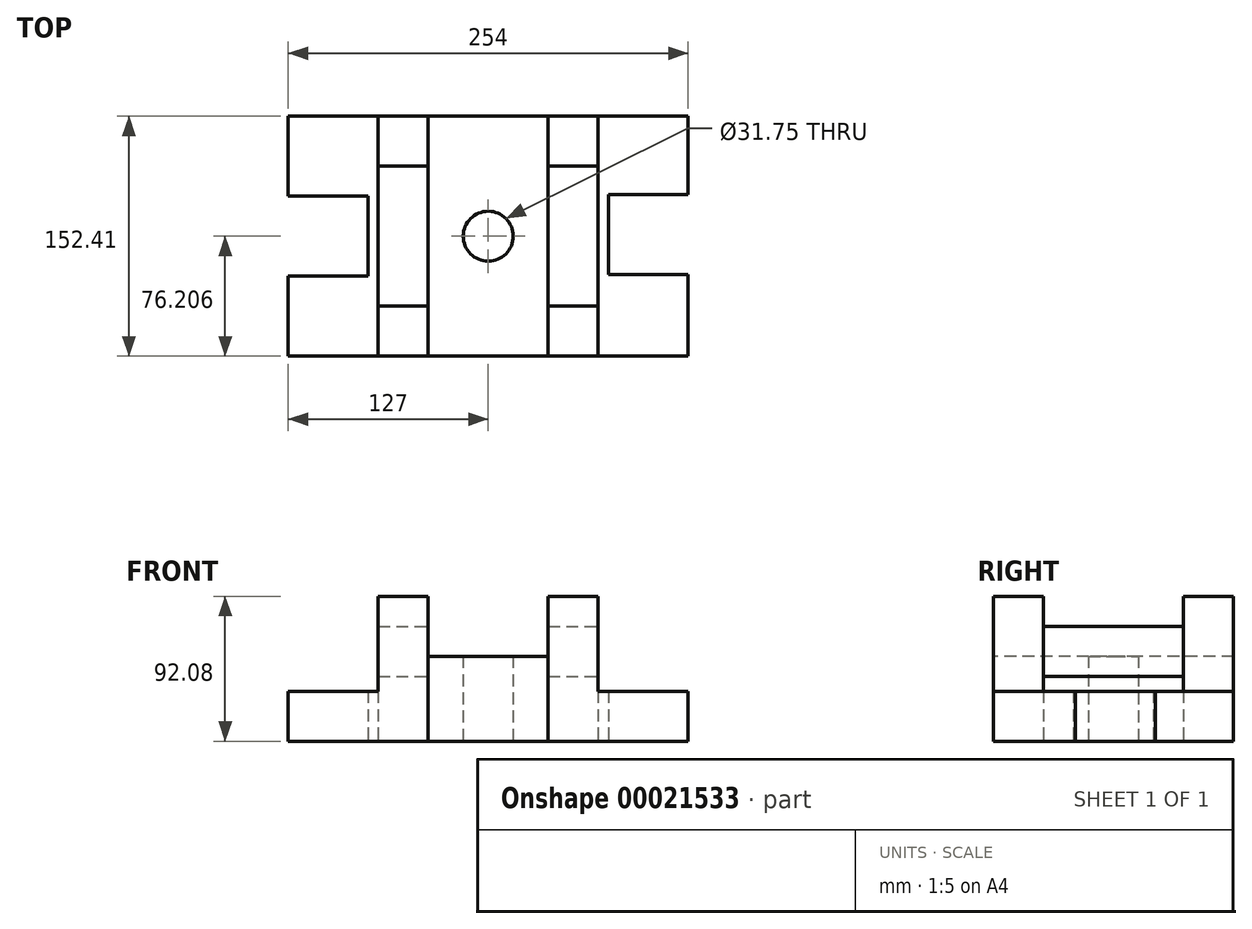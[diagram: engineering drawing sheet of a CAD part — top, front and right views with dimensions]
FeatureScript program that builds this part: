
annotation { "Feature Type Name" : "Feature", "Feature Type Description" : "" }
export const myFeature = defineFeature(function(context is Context, id is Id, definition is map)
    precondition{}
    {
        {
            var Q0;
            Q0=qCreatedBy(makeId("Top.planeOp"),FACE);
            var sketch = newSketch(context, id + "F0", { "sketchPlane" : qUnion([Q0])});
            skLineSegment(sketch, "E0.bottom", {"start": v(69.85, 100.56) * mm, "end": v(127, 100.56) * mm});
            skLineSegment(sketch, "E0.top", {"start": v(0, -51.84) * mm, "end": v(127, -51.84) * mm});
            skLineSegment(sketch, "E0.right", {"start": v(127, 100.56) * mm, "end": v(127, -51.84) * mm});
            skLineSegment(sketch, "E1", {"start": v(127, 50.8) * mm, "end": v(76.38, 50.8) * mm});
            skLineSegment(sketch, "E2", {"start": v(76.38, 50.8) * mm, "end": v(76.38, 0) * mm});
            skLineSegment(sketch, "E3", {"start": v(76.38, 0) * mm, "end": v(127, 0) * mm});
            skLineSegment(sketch, "E4", {"start": v(38.1, 68.8) * mm, "end": v(38.1, -20.1) * mm});
            skLineSegment(sketch, "E5", {"start": v(69.85, 68.8) * mm, "end": v(69.85, -20.1) * mm});
            skLineSegment(sketch, "E6", {"start": v(0, 100.56) * mm, "end": v(38.1, 100.56) * mm});
            skLineSegment(sketch, "E7", {"start": v(38.1, 100.56) * mm, "end": v(69.85, 100.56) * mm});
            skLineSegment(sketch, "E8.MirrorCS", {"start": v(0, 100.55) * mm, "end": v(-38.1, 100.55) * mm});
            skLineSegment(sketch, "E9.MirrorCS", {"start": v(-38.1, 68.8) * mm, "end": v(-38.1, -20.1) * mm});
            skLineSegment(sketch, "E10.MirrorCS", {"start": v(-69.85, 68.8) * mm, "end": v(-69.85, -20.1) * mm});
            skLineSegment(sketch, "E11.MirrorCS", {"start": v(0, -51.85) * mm, "end": v(-127, -51.85) * mm});
            skLineSegment(sketch, "E12.MirrorCS", {"start": v(-127, 100.55) * mm, "end": v(-127, 100.55) * mm});
            skLineSegment(sketch, "E13.MirrorCS", {"start": v(-76.38, 50.8) * mm, "end": v(-76.38, -0.9) * mm});
            skLineSegment(sketch, "E14.MirrorCS", {"start": v(-127, 49.75) * mm, "end": v(-76.38, 49.75) * mm});
            skLineSegment(sketch, "E15.MirrorCS", {"start": v(-69.85, 100.55) * mm, "end": v(-127, 100.55) * mm});
            skLineSegment(sketch, "E16", {"start": v(0, -51.84) * mm, "end": v(0, 24.36) * mm});
            skLineSegment(sketch, "E17", {"start": v(-69.85, 68.8) * mm, "end": v(-38.1, 68.8) * mm});
            skLineSegment(sketch, "E18", {"start": v(38.1, 68.8) * mm, "end": v(69.85, 68.8) * mm});
            skLineSegment(sketch, "E19", {"start": v(-69.85, -20.1) * mm, "end": v(-38.1, -20.1) * mm});
            skLineSegment(sketch, "E20", {"start": v(38.1, -20.1) * mm, "end": v(69.85, -20.1) * mm});
            skLineSegment(sketch, "E21", {"start": v(38.1, 100.56) * mm, "end": v(38.1, 68.8) * mm});
            skLineSegment(sketch, "E22", {"start": v(69.85, 100.56) * mm, "end": v(69.85, 68.8) * mm});
            skLineSegment(sketch, "E23", {"start": v(38.1, -20.1) * mm, "end": v(38.1, -51.84) * mm});
            skLineSegment(sketch, "E24", {"start": v(69.85, -20.1) * mm, "end": v(69.85, -51.84) * mm});
            skLineSegment(sketch, "E25", {"start": v(-69.85, 100.55) * mm, "end": v(-69.85, 68.8) * mm});
            skLineSegment(sketch, "E26", {"start": v(-38.1, 100.55) * mm, "end": v(-38.1, 68.8) * mm});
            skLineSegment(sketch, "E27", {"start": v(-38.1, -20.1) * mm, "end": v(-38.1, -51.85) * mm});
            skLineSegment(sketch, "E28", {"start": v(-69.85, -20.1) * mm, "end": v(-69.85, -51.85) * mm});
            skLineSegment(sketch, "E29.trimOffspring", {"start": v(-127, 49.75) * mm, "end": v(-127, -1.05) * mm});
            skLineSegment(sketch, "E30", {"start": v(-127, 100.55) * mm, "end": v(-127, 49.75) * mm});
            skLineSegment(sketch, "E31", {"start": v(-127, -1.05) * mm, "end": v(-127, -51.85) * mm});
            skLineSegment(sketch, "E32", {"start": v(-69.85, 100.55) * mm, "end": v(-38.1, 100.55) * mm});
            skLineSegment(sketch, "E33", {"start": v(-76.38, 49.75) * mm, "end": v(-69.85, 49.75) * mm});
            skLineSegment(sketch, "E34", {"start": v(-76.38, -0.9) * mm, "end": v(-69.85, -0.9) * mm});
            skLineSegment(sketch, "E35", {"start": v(-145.92, 92.06) * mm, "end": v(-145.92, 94.46) * mm});
            skLineSegment(sketch, "E36", {"start": v(-76.38, -0.9) * mm, "end": v(-127, -1.05) * mm});
            skLineSegment(sketch, "E37.bottom", {"start": v(-38.1, 100.55) * mm, "end": v(38.1, 100.55) * mm});
            skLineSegment(sketch, "E37.top", {"start": v(-38.1, -51.84) * mm, "end": v(38.1, -51.84) * mm});
            skLineSegment(sketch, "E37.left", {"start": v(-38.1, 100.55) * mm, "end": v(-38.1, -51.84) * mm});
            skLineSegment(sketch, "E37.right", {"start": v(38.1, 100.55) * mm, "end": v(38.1, -51.84) * mm});
            skCircle(sketch, "E38", {"center": v(0, 24.36) * mm, "radius": 15.88 * mm});
            skSolve(sketch);
        }
        {
            var Q0;
            {var subQ6=sQuery(id+"F0.wireOp",EDGE,"E0.bottom");Q0=makeQuery(id+"F0.imprint","IMPRINT",FACE,{"disambiguationData":[TD([[makeQuery(id+"F0.imprint","IMPRINT",EDGE,{"derivedFrom":subQ6}),-1.0]])]});}
            extrude(context, id + "F1", {"entities" : qUnion([Q0]), "depth" : 31.75 * mm});
        }
        {
            var Q0;
            Q0=makeQuery(id+"F0.imprint","IMPRINT",FACE,{"disambiguationData":[TD([[makeQuery(id+"F0.imprint","IMPRINT",EDGE,{"derivedFrom":sQuery(id+"F0.wireOp",EDGE,"E20")}),-1.0]])]});
            var Q1;
            Q1=makeQuery(id+"F0.imprint","IMPRINT",FACE,{"disambiguationData":[TD([[makeQuery(id+"F0.imprint","IMPRINT",EDGE,{"derivedFrom":sQuery(id+"F0.wireOp",EDGE,"E7")}),-1.0]])]});
            extrude(context, id + "F2", {"entities" : qUnion([Q0, Q1]), "operationType" : NewBodyOperationType.ADD, "depth" : 92.07 * mm});
        }
        {
            var Q0;
            Q0=makeQuery(id+"F0.imprint","IMPRINT",FACE,{"disambiguationData":[TD([[makeQuery(id+"F0.imprint","IMPRINT",EDGE,{"derivedFrom":sQuery(id+"F0.wireOp",EDGE,"E4")}),1.0]])]});
            extrude(context, id + "F3", {"entities" : qUnion([Q0]), "operationType" : NewBodyOperationType.ADD, "depth" : 41.27 * mm});
        }
        {
            var Q0;
            Q0=makeQuery(id+"F0.imprint","IMPRINT",FACE,{"disambiguationData":[TD([[makeQuery(id+"F0.imprint","IMPRINT",EDGE,{"derivedFrom":sQuery(id+"F0.wireOp",EDGE,"E15.MirrorCS")}),1.0]])]});
            var Q1;
            {var subQ1=sQuery(id+"F0.wireOp",EDGE,"E33");Q1=makeQuery(id+"F0.imprint","IMPRINT",FACE,{"disambiguationData":[TD([[makeQuery(id+"F0.imprint","IMPRINT",EDGE,{"derivedFrom":subQ1}),-1.0]])]});}
            var Q2;
            {var subQ2=sQuery(id+"F0.wireOp",EDGE,"E28");Q2=makeQuery(id+"F0.imprint","IMPRINT",FACE,{"disambiguationData":[TD([[makeQuery(id+"F0.imprint","IMPRINT",EDGE,{"derivedFrom":subQ2}),-1.0]])]});}
            extrude(context, id + "F4", {"entities" : qUnion([Q0, Q1, Q2]), "depth" : 31.75 * mm});
        }
        {
            var Q0;
            Q0=makeQuery(id+"F0.imprint","IMPRINT",FACE,{"disambiguationData":[TD([[makeQuery(id+"F0.imprint","IMPRINT",EDGE,{"derivedFrom":sQuery(id+"F0.wireOp",EDGE,"E17")}),1.0]])]});
            var Q1;
            Q1=makeQuery(id+"F0.imprint","IMPRINT",FACE,{"disambiguationData":[TD([[makeQuery(id+"F0.imprint","IMPRINT",EDGE,{"derivedFrom":sQuery(id+"F0.wireOp",EDGE,"E19")}),-1.0]])]});
            extrude(context, id + "F5", {"entities" : qUnion([Q0, Q1]), "operationType" : NewBodyOperationType.ADD, "depth" : 92.07 * mm});
        }
        {
            var Q0;
            Q0=makeQuery(id+"F0.imprint","IMPRINT",FACE,{"disambiguationData":[TD([[makeQuery(id+"F0.imprint","IMPRINT",EDGE,{"derivedFrom":sQuery(id+"F0.wireOp",EDGE,"E9.MirrorCS")}),-1.0]])]});
            extrude(context, id + "F6", {"entities" : qUnion([Q0]), "operationType" : NewBodyOperationType.ADD, "depth" : 41.27 * mm});
        }
        {
            var Q0;
            {var subQ2=sQuery(id+"F0.wireOp",EDGE,"E37.top");var subQ11=makeQuery(id+"F0.imprint","IMPRINT",VERTEX,{"derivedFrom":subQ2});Q0=makeQuery(id+"F0.imprint","IMPRINT",FACE,{"disambiguationData":[TD([[makeQuery(id+"F0.imprint","IMPRINT",EDGE,{"disambiguationData":[TD([[subQ11,1.0]])],"derivedFrom":subQ2}),1.0]])]});}
            extrude(context, id + "F7", {"entities" : qUnion([Q0]), "depth" : 53.97 * mm});
        }
        {
            var Q0;
            {var subQ2=sQuery(id+"F0.wireOp",EDGE,"E17");Q0=makeQuery(id+"F0.imprint","IMPRINT",FACE,{"disambiguationData":[TD([[makeQuery(id+"F0.imprint","IMPRINT",EDGE,{"derivedFrom":subQ2}),-1.0]])]});}
            extrude(context, id + "F8", {"entities" : qUnion([Q0]), "depth" : 73.02 * mm});
        }
        {
            var Q0;
            Q0=makeQuery(id+"F0.imprint","IMPRINT",FACE,{"disambiguationData":[TD([[makeQuery(id+"F0.imprint","IMPRINT",EDGE,{"derivedFrom":sQuery(id+"F0.wireOp",EDGE,"E5")}),-1.0]])]});
            extrude(context, id + "F9", {"entities" : qUnion([Q0]), "depth" : 73.02 * mm});
        }
    });
